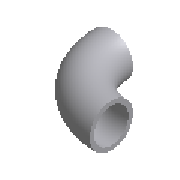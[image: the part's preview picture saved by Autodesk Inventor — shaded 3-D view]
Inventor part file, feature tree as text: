
AUTODESK INVENTOR PART (.ipt)
format: ipt  version: 2025.3 (Build 293356030, 356C)  size: 183,296 bytes
history: native  units: mm (DEFAULTED — no unit token found)
features: other x4, sweep x1
ambient origin geometry x8: Origin, YZ Plane, XZ Plane, XY Plane, X Axis, Y Axis, Z Axis, Center Point
bodies: Solid1 (feature_tree)
feature tree (5):
  sweep  "Sweep1"
  other  "Work Point1"
  other  "Work Point2"
  other  "Work Axis1"
  other  "Work Axis2"
